# Revit family: DTI_A3-AC-Panel-A21-Frame-Fs3
name_source: partatom
category: Doors
revit_build: Autodesk Revit 2016 (Build: 20150220_1215(x64)
units: mm (PartAtom-declared; Revit-internal decimal feet)

## family parameters
Always vertical = Yes
Cut with Voids When Loaded = No
Host = Wall
Room Calculation Point = No
Shared = No

## types (1)
- Panel A21 - Frame FS3
    Assembly Code = B2030230
    Frame Depth = 47 mm  [stored 0.154199 ft]
    Frame Material = Meranti Wood
    Frame Thickness = 102 mm
    Frame Type = Frame FS3
    Function = Interior
    Height = 2100 mm
    Manufacturer = AC Doors
    Manufacturer Code = A21 - FS3
    Model = Double-sided Panel Door
    Panel Height = 2053 mm
    Panel Material = Meranti Wood
    Panel Thickness = 44 mm  [stored 0.144357 ft]
    Panel Type = A21
    Panel Width = 895 mm  [stored 2.93635 ft]
    Sidelight Glass = Glass
    Sidelight w = 371 mm  [stored 1.21719 ft]
    URL = www.acdoors.co.za
    Wall Closure = By host
    Width = 1360 mm  [stored 4.46194 ft]

note: [stored X ft] marks values corroborated as IEEE doubles in the binary element streams (Revit-internal decimal feet)

## geometry (parser evidence)
native form markers: Sweep x8
no freeform markers — native parametric forms only
